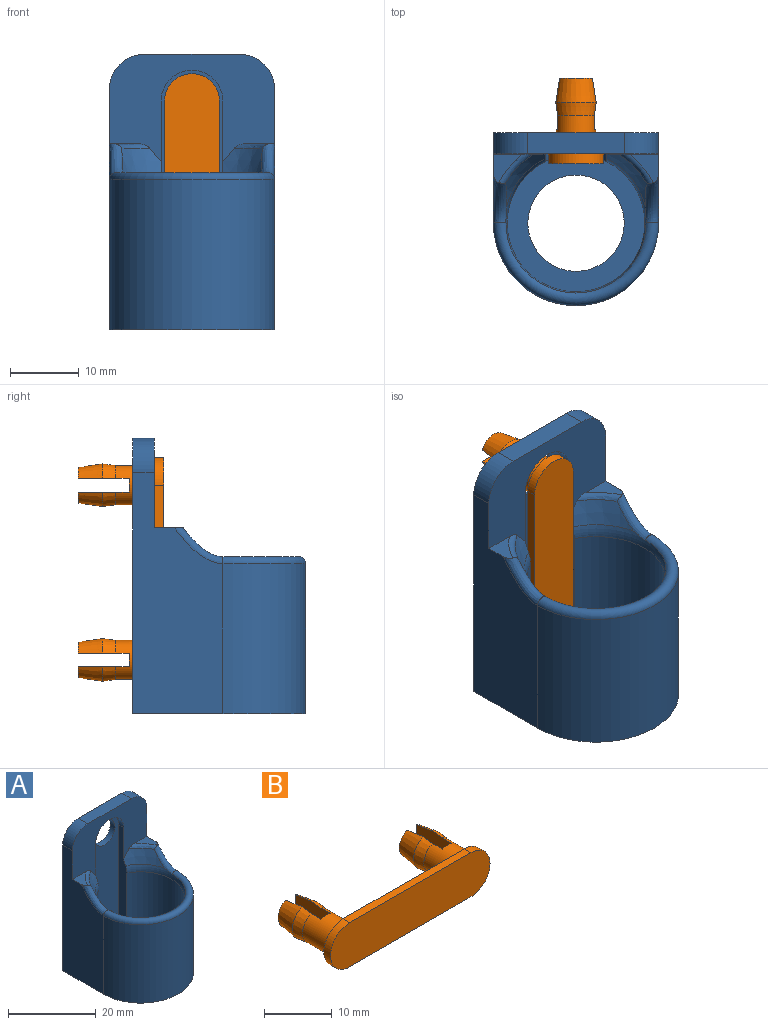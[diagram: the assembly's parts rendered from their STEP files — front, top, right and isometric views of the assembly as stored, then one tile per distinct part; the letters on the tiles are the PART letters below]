
ASSEMBLY  parts=2 mates=1
PART A: 29 faces, bbox 26.1x26.3x40.2 mm
  f0: cone r=10mm half-angle=21.8deg, axis (0,0,1), area 30.2mm2, adj f2,f3,f7,f15,f21
  f1: cone r=10mm half-angle=21.8deg, axis (0,0,1), area 30.2mm2, adj f2,f3,f6,f14,f20
  f2: torus R=15mm, axis (0,0,-1), area 84.9mm2, adj f0,f1,f11,f13,f14,f15,f20,f21
  f3: plane 24.13x15.69mm, normal (0,-1,0), area 219.6mm2, adj f0,f1,f4,f5,f6,f7,f8,f10
  f4: plane 4.38x4.31mm, normal (0,0,1), area 9.1mm2, adj f3,f7,f10,f15
  f5: plane 4.38x4.31mm, normal (0,0,1), area 9.1mm2, adj f3,f6,f8,f14
  f6: torus R=12.68mm, axis (0,0,1), area 6.7mm2, adj f1,f3,f5,f14
  f7: torus R=12.68mm, axis (0,0,1), area 6.7mm2, adj f0,f3,f4,f15
  f8: plane 35x13.12mm, normal (-1,0,0), area 354.8mm2, adj f3,f5,f9,f12,f14,f24,f28
  f9: cylinder r=12mm len=24mm, axis (0,0,1), area 822.1mm2, adj f8,f10,f13,f28
  f10: plane 35x13.12mm, normal (1,0,0), area 354.8mm2, adj f3,f4,f9,f12,f15,f25,f28
  f11: cylinder r=10mm len=20mm, axis (0,0,1), area 1072.6mm2, adj f2,f19,f20,f21,f26
  f12: plane 40x24mm, normal (0,1,0), area 878.8mm2, adj f8,f10,f16,f22,f23,f24,f25,f28
  f13: torus R=11mm, axis (0,0,-1), area 89mm2, adj f2,f9,f14,f15
  f14: bspline ~8.92x7.57mm, area 20.2mm2, adj f1,f2,f5,f6,f8,f13
  f15: bspline ~7.98x7.57mm, area 20.2mm2, adj f0,f2,f4,f7,f10,f13
  f16: plane 14x3.1mm, normal (0,0,1), area 43.4mm2, adj f3,f12,f24,f25
  f17: plane 34.4x9mm, normal (0,-1,0), area 221.7mm2, adj f18,f19,f20,f21,f22,f23
  f18: cylinder r=4.5mm len=9mm, axis (0,1,0), area 22.6mm2, adj f3,f17,f20,f21
  f19: cylinder r=4.5mm len=9mm, axis (0,1,0), area 37.9mm2, adj f11,f17,f20,f21
  f20: plane 25.48x2.77mm, normal (1,0,0), area 57.3mm2, adj f1,f2,f3,f11,f17,f18,f19
  f21: plane 25.48x2.77mm, normal (-1,0,0), area 57.3mm2, adj f0,f2,f3,f11,f17,f18,f19
  f22: cylinder r=3.35mm len=6.7mm, axis (0,-1,0), area 31.6mm2, adj f12,f17
  f23: cylinder r=3.35mm len=6.7mm, axis (0,-1,0), area 31.6mm2, adj f12,f17
  f24: cylinder r=5mm len=5mm, axis (0,1,0), area 24.3mm2, adj f3,f8,f12,f16
  f25: cylinder r=5mm len=5mm, axis (0,-1,0), area 24.3mm2, adj f3,f10,f12,f16
  f26: plane 20x20mm, normal (0,0,1), area 160.2mm2, adj f11,f27
  f27: cylinder r=7mm len=14mm, axis (0,0,1), area 88mm2, adj f26,f28
  f28: plane 25.11x24mm, normal (0,0,-1), area 387mm2, adj f8,f9,f10,f12,f27
PART B: 26 faces, bbox 33.4x12.4x8 mm
  f0: cylinder r=2.85mm len=5.7mm, axis (0,-1,0), area 92.1mm2, adj f7,f12,f19,f20,f21,f22
  f1: cylinder r=2.85mm len=5.7mm, axis (0,-1,0), area 92.1mm2, adj f4,f12,f16,f23,f24,f25
  f2: plane 4.8x1.6mm, normal (0,1,0), area 5.5mm2, adj f15,f25
  f3: cone r=3.1mm half-angle=8.1deg, axis (0,-1,0), area 24.4mm2, adj f4,f14,f24
  f4: cone r=2.85mm half-angle=7.5deg, axis (0,1,0), area 14mm2, adj f1,f3,f24
  f5: plane 4.8x1.6mm, normal (0,1,0), area 5.5mm2, adj f18,f22
  f6: cone r=3.1mm half-angle=8.1deg, axis (0,-1,0), area 24.4mm2, adj f7,f17,f21
  f7: cone r=2.85mm half-angle=7.5deg, axis (0,1,0), area 14mm2, adj f0,f6,f21
  f8: cylinder r=4mm len=8mm, axis (0,-1,0), area 17.6mm2, adj f9,f11,f12,f13
  f9: plane 25.4x1.4mm, normal (0,0,-1), area 35.6mm2, adj f8,f10,f12,f13
  f10: cylinder r=4mm len=8mm, axis (0,-1,0), area 17.6mm2, adj f9,f11,f12,f13
  f11: plane 25.4x1.4mm, normal (0,0,1), area 35.6mm2, adj f8,f10,f12,f13
  f12: plane 33.4x8mm, normal (0,1,0), area 202.4mm2, adj f0,f1,f8,f9,f10,f11
  f13: plane 33.4x8mm, normal (0,-1,0), area 253.5mm2, adj f8,f9,f10,f11
  f14: plane 4.8x1.6mm, normal (0,1,0), area 5.5mm2, adj f3,f24
  f15: cone r=3.1mm half-angle=8.1deg, axis (0,-1,0), area 24.4mm2, adj f2,f16,f25
  f16: cone r=2.85mm half-angle=7.5deg, axis (0,1,0), area 14mm2, adj f1,f15,f25
  f17: plane 4.8x1.6mm, normal (0,1,0), area 5.5mm2, adj f6,f21
  f18: cone r=3.1mm half-angle=8.1deg, axis (0,-1,0), area 24.4mm2, adj f5,f19,f22
  f19: cone r=2.85mm half-angle=7.5deg, axis (0,1,0), area 14mm2, adj f0,f18,f22
  f20: plane 5.7x2mm, normal (0,1,0), area 11.2mm2, adj f0,f21,f22
  f21: plane 7.42x5.89mm, normal (1,0,0), area 40mm2, adj f0,f6,f7,f17,f20
  f22: plane 7.42x5.89mm, normal (-1,0,0), area 40mm2, adj f0,f5,f18,f19,f20
  f23: plane 5.7x2mm, normal (0,1,0), area 11.2mm2, adj f1,f24,f25
  f24: plane 7.42x5.89mm, normal (1,0,0), area 40mm2, adj f1,f3,f4,f14,f23
  f25: plane 7.42x5.89mm, normal (-1,0,0), area 40mm2, adj f1,f2,f15,f16,f23
PLACE A t=(0,0,-6.5)mm
PLACE B rot(axis=(0,1,0),90deg) t=(-31.75,-4.5,-13)mm
MATE fastened B.f0 <-> A.f18  axis (0,1,0) through (0,-3.1,-0.3)mm
